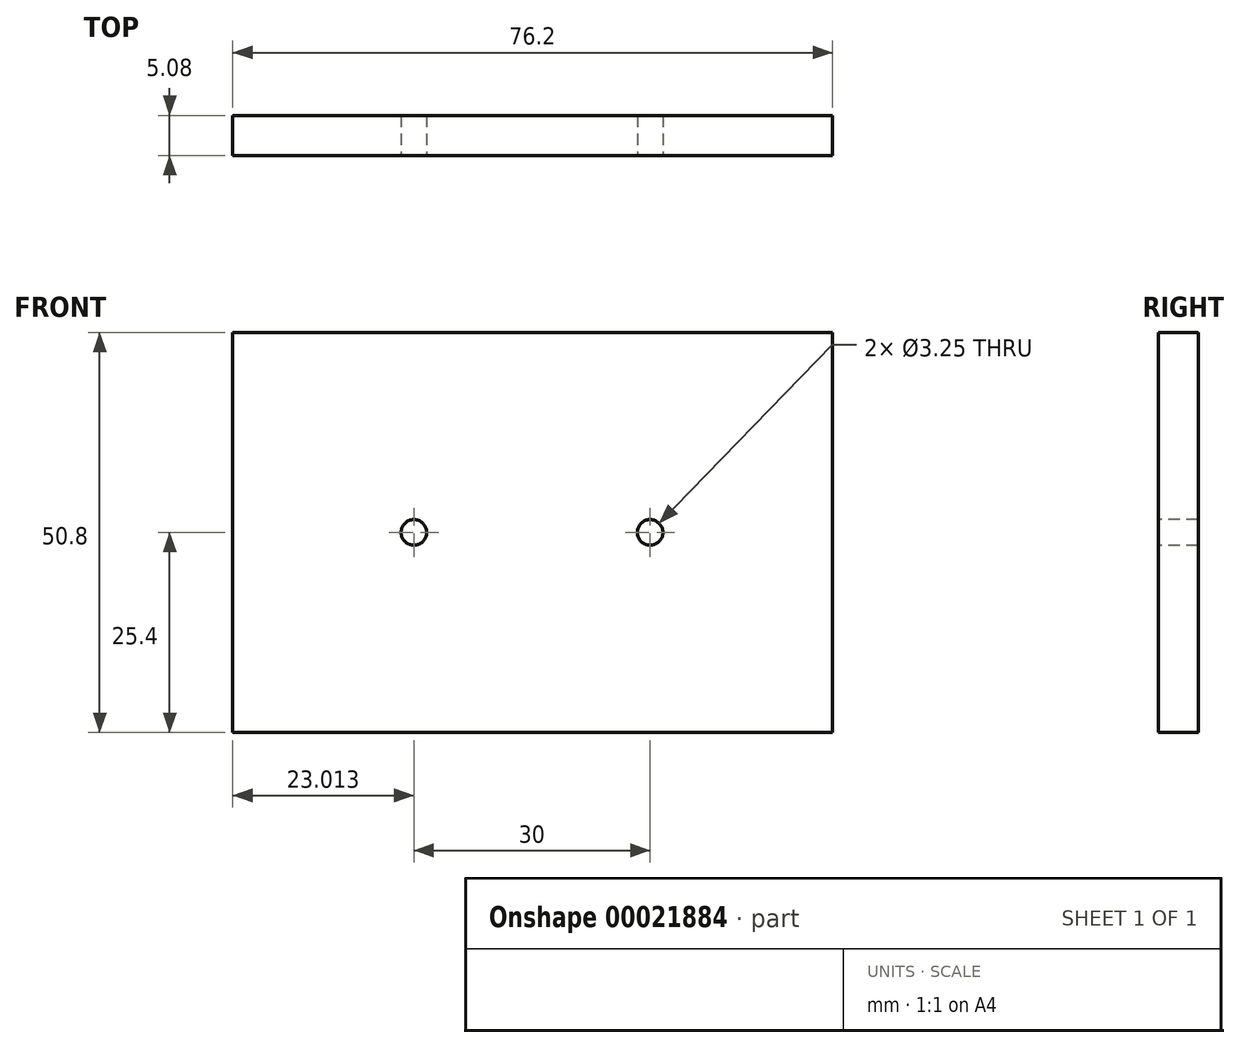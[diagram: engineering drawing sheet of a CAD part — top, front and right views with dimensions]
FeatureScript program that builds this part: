
annotation { "Feature Type Name" : "Feature", "Feature Type Description" : "" }
export const myFeature = defineFeature(function(context is Context, id is Id, definition is map)
    precondition{}
    {
        {
            var Q0;
            Q0=qCreatedBy(makeId("Front.planeOp"),FACE);
            var sketch = newSketch(context, id + "F0", { "sketchPlane" : qUnion([Q0])});
            skLineSegment(sketch, "E0.rect.bottom", {"start": v(38.1, -25.4) * mm, "end": v(-38.1, -25.4) * mm});
            skLineSegment(sketch, "E0.rect.top", {"start": v(38.1, 25.4) * mm, "end": v(-38.1, 25.4) * mm});
            skLineSegment(sketch, "E0.rect.left", {"start": v(38.1, -25.4) * mm, "end": v(38.1, 25.4) * mm});
            skLineSegment(sketch, "E0.rect.right", {"start": v(-38.1, -25.4) * mm, "end": v(-38.1, 25.4) * mm});
            skPoint(sketch, "E0.rect.middle", {"position": v(0, 0) * mm});
            skSolve(sketch);
        }
        {
            var Q0;
            Q0 = qSketchRegion(id + "F0", true);
            extrude(context, id + "F1", {"entities" : qUnion([Q0]), "depth" : 5.08 * mm});
        }
        {
            var Q0;
            Q0=makeQuery(id+"F1.opExtrude","CAP_FACE",FACE,{"disambiguationData":[OSD([sQuery(id+"F0.wireOp",EDGE,"E0.rect.bottom"),sQuery(id+"F0.wireOp",EDGE,"E0.rect.top"),sQuery(id+"F0.wireOp",EDGE,"E0.rect.left"),sQuery(id+"F0.wireOp",EDGE,"E0.rect.right")])],"isStart":false});
            var sketch = newSketch(context, id + "F2", { "sketchPlane" : qUnion([Q0])});
            skPoint(sketch, "E1", {"position": v(-15.09, 0) * mm});
            skPoint(sketch, "E2", {"position": v(14.91, 0) * mm});
            skSolve(sketch);
        }
        {
            var Q0;
            Q0=sQuery(id+"F2.wireOp",VERTEX,"E1");
            var Q1;
            Q1=sQuery(id+"F2.wireOp",VERTEX,"E2");
            var Q2;
            Q2=makeQuery(id+"F1.opExtrude","SWEPT_BODY",BODY,{"disambiguationData":[OSD([sQuery(id+"F0.wireOp",EDGE,"E0.rect.bottom"),sQuery(id+"F0.wireOp",EDGE,"E0.rect.top"),sQuery(id+"F0.wireOp",EDGE,"E0.rect.left"),sQuery(id+"F0.wireOp",EDGE,"E0.rect.right")])]});
            hole(context, id + "F3", {"style" : HoleStyle.SIMPLE, "holeDiameter" : 3.25 * mm, "endStyle" : HoleEndStyle.THROUGH, "locations" : qUnion([Q0, Q1]), "scope" : qUnion([Q2])});
        }
    });
